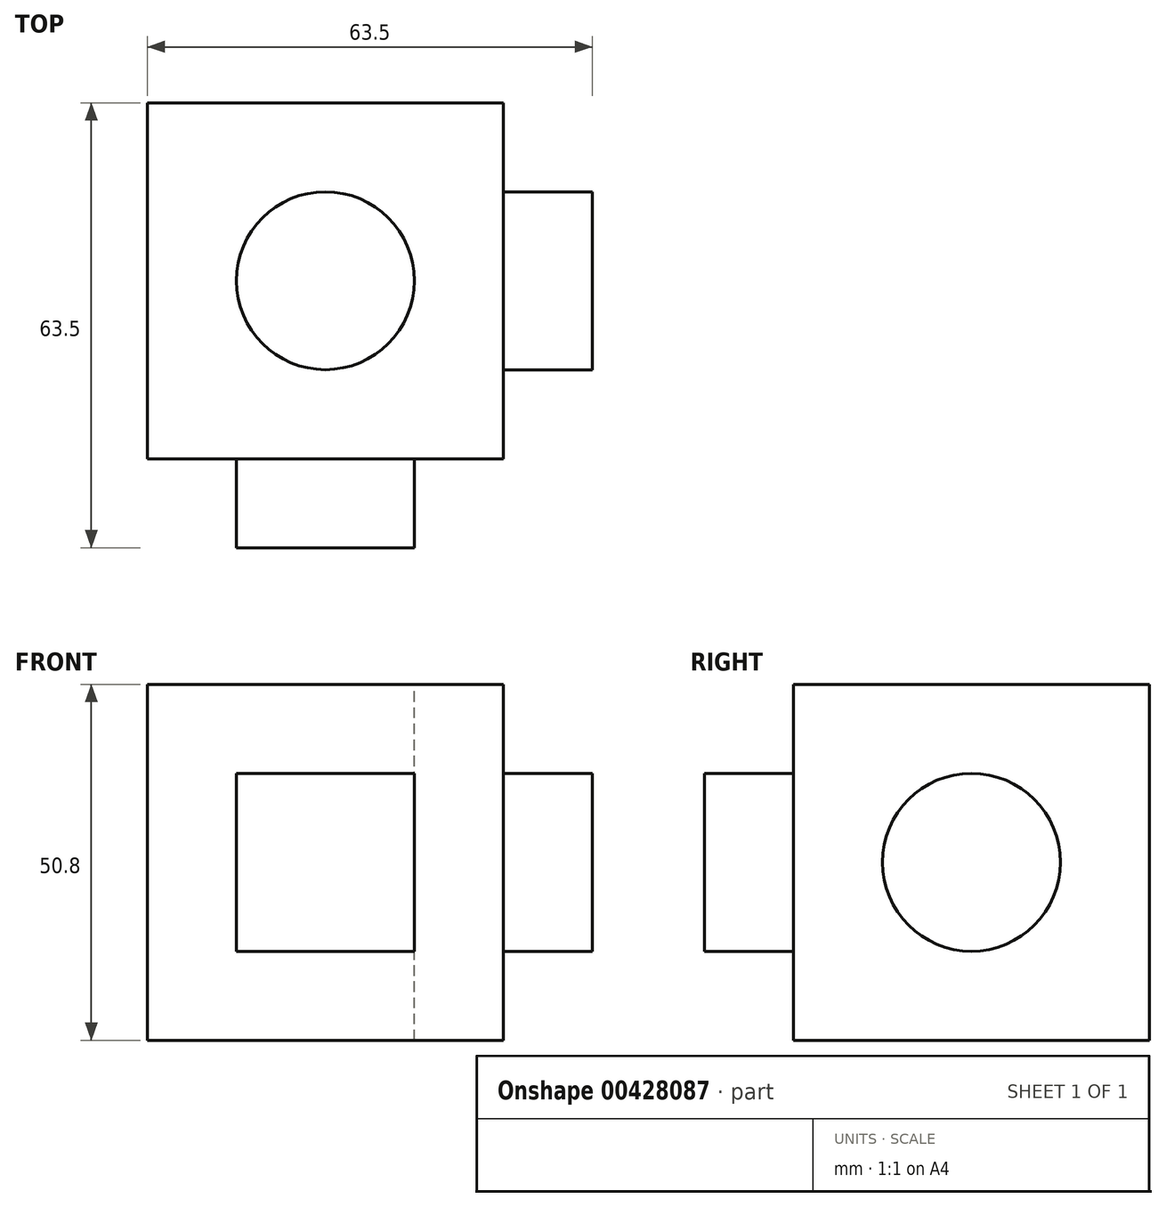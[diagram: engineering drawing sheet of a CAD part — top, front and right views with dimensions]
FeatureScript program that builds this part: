
annotation { "Feature Type Name" : "Feature", "Feature Type Description" : "" }
export const myFeature = defineFeature(function(context is Context, id is Id, definition is map)
    precondition{}
    {
        {
            var Q0;
            Q0=qCreatedBy(makeId("Front.planeOp"),FACE);
            var sketch = newSketch(context, id + "F0", { "sketchPlane" : qUnion([Q0])});
            skLineSegment(sketch, "E0.bottom", {"start": v(0, 0) * mm, "end": v(-50.8, 0) * mm});
            skLineSegment(sketch, "E0.top", {"start": v(0, 50.8) * mm, "end": v(-50.8, 50.8) * mm});
            skLineSegment(sketch, "E0.left", {"start": v(0, 0) * mm, "end": v(0, 50.8) * mm});
            skLineSegment(sketch, "E0.right", {"start": v(-50.8, 0) * mm, "end": v(-50.8, 50.8) * mm});
            skSolve(sketch);
        }
        {
            var Q0;
            Q0=makeQuery(id+"F0.imprint","IMPRINT",FACE,{"disambiguationData":[TD([[makeQuery(id+"F0.imprint","IMPRINT",EDGE,{"derivedFrom":sQuery(id+"F0.wireOp",EDGE,"E0.bottom")}),-1.0]])]});
            extrude(context, id + "F1", {"entities" : qUnion([Q0]), "depth" : 50.8 * mm});
        }
        {
            var Q0;
            Q0=makeQuery(id+"F1.opExtrude","SWEPT_FACE",FACE,{"disambiguationData":[OSD([sQuery(id+"F0.wireOp",EDGE,"E0.top")])]});
            var sketch = newSketch(context, id + "F2", { "sketchPlane" : qUnion([Q0])});
            skCircle(sketch, "E1", {"center": v(-25.4, -25.4) * mm, "radius": 12.7 * mm});
            skSolve(sketch);
        }
        {
            var Q0;
            Q0=makeQuery(id+"F2.imprint","IMPRINT",FACE,{"disambiguationData":[TD([[makeQuery(id+"F2.imprint","IMPRINT",EDGE,{"derivedFrom":sQuery(id+"F2.wireOp",EDGE,"E1")}),1.0]])]});
            extrude(context, id + "F3", {"entities" : qUnion([Q0]), "operationType" : NewBodyOperationType.REMOVE, "oppositeDirection" : true, "depth" : 50.8 * mm});
        }
        {
            var Q0;
            Q0=makeQuery(id+"F1.opExtrude","CAP_FACE",FACE,{"disambiguationData":[OSD([sQuery(id+"F0.wireOp",EDGE,"E0.bottom"),sQuery(id+"F0.wireOp",EDGE,"E0.top"),sQuery(id+"F0.wireOp",EDGE,"E0.left"),sQuery(id+"F0.wireOp",EDGE,"E0.right")])],"isStart":false});
            var sketch = newSketch(context, id + "F4", { "sketchPlane" : qUnion([Q0])});
            skLineSegment(sketch, "E2.bottom", {"start": v(-38.1, 38.1) * mm, "end": v(-12.7, 38.1) * mm});
            skLineSegment(sketch, "E2.top", {"start": v(-38.1, 12.7) * mm, "end": v(-12.7, 12.7) * mm});
            skLineSegment(sketch, "E2.left", {"start": v(-38.1, 38.1) * mm, "end": v(-38.1, 12.7) * mm});
            skLineSegment(sketch, "E2.right", {"start": v(-12.7, 38.1) * mm, "end": v(-12.7, 12.7) * mm});
            skSolve(sketch);
        }
        {
            var Q0;
            Q0 = qSketchRegion(id + "F4", true);
            extrude(context, id + "F5", {"entities" : qUnion([Q0]), "operationType" : NewBodyOperationType.ADD, "depth" : 12.7 * mm});
        }
        {
            var Q0;
            Q0=makeQuery(id+"F1.opExtrude","SWEPT_FACE",FACE,{"disambiguationData":[OSD([sQuery(id+"F0.wireOp",EDGE,"E0.left")])]});
            var sketch = newSketch(context, id + "F6", { "sketchPlane" : qUnion([Q0])});
            skCircle(sketch, "E3", {"center": v(-25.4, 25.4) * mm, "radius": 12.7 * mm});
            skSolve(sketch);
        }
        {
            var Q0;
            Q0 = qSketchRegion(id + "F6", true);
            extrude(context, id + "F7", {"entities" : qUnion([Q0]), "operationType" : NewBodyOperationType.ADD, "depth" : 12.7 * mm});
        }
    });
